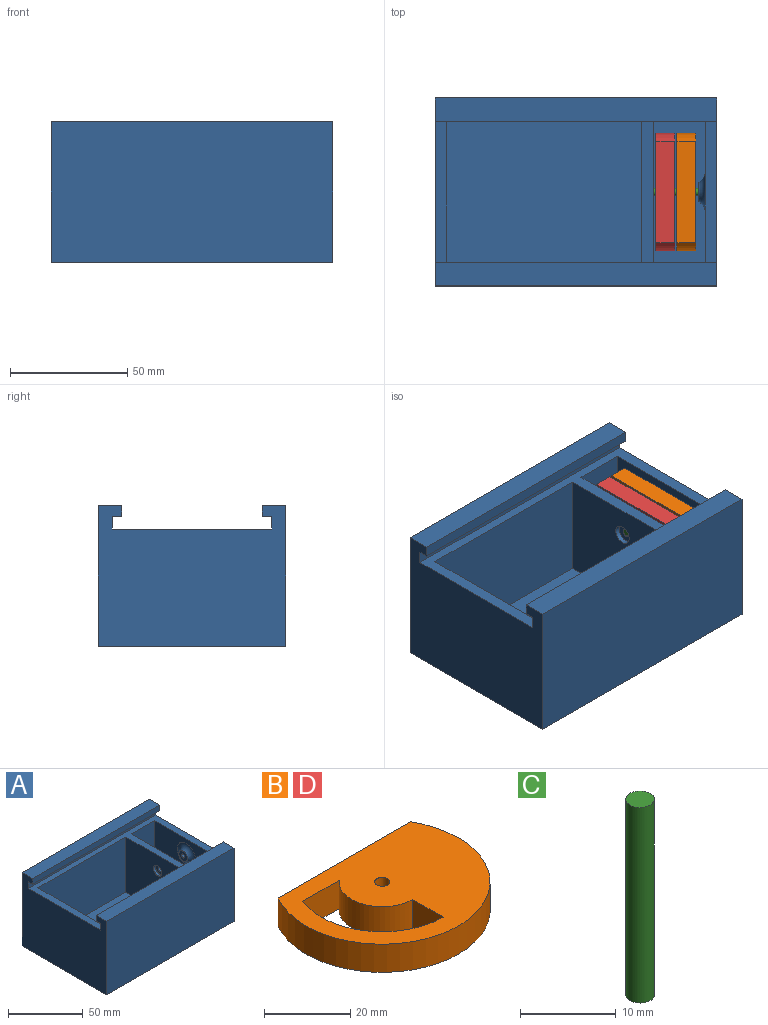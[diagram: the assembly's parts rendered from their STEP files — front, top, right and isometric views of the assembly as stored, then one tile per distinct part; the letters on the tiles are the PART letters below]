
ASSEMBLY  parts=4 mates=3
PART A: 31 faces, bbox 120x80x60 mm
  f0: cylinder r=1.6mm len=3.2mm, axis (-1,0,0), area 30.2mm2, adj f14,f30
  f1: plane 83x45mm, normal (0,1,0), area 3735mm2, adj f7,f9,f13,f15
  f2: plane 45x22mm, normal (0,1,0), area 990mm2, adj f10,f11,f13,f14
  f3: plane 120x4.6mm, normal (0,1,0), area 552mm2, adj f4,f12,f17,f23
  f4: plane 80x60mm, normal (-1,0,0), area 4156.8mm2, adj f3,f8,f13,f16,f17,f18,f19,f20
  f5: plane 83x45mm, normal (0,-1,0), area 3735mm2, adj f7,f9,f13,f15
  f6: plane 45x22mm, normal (0,-1,0), area 990mm2, adj f10,f11,f13,f14
  f7: plane 83x60mm, normal (0,0,1), area 4980mm2, adj f1,f5,f9,f15
  f8: plane 120x80mm, normal (0,0,-1), area 9600mm2, adj f4,f12,f16,f19
  f9: plane 60x45mm, normal (-1,0,0), area 2649.7mm2, adj f1,f5,f7,f13,f29
  f10: plane 60x22mm, normal (0,0,1), area 1320mm2, adj f2,f6,f11,f14
  f11: plane 60x45mm, normal (-1,0,0), area 2468.6mm2, adj f2,f6,f10,f13,f28
  f12: plane 80x60mm, normal (1,0,0), area 4156.8mm2, adj f3,f8,f13,f16,f17,f18,f19,f20
  f13: plane 120x68mm, normal (0,0,1), area 1860mm2, adj f1,f2,f4,f5,f6,f9,f11,f12
  f14: plane 60x45mm, normal (1,0,0), area 2692mm2, adj f0,f2,f6,f10,f13
  f15: plane 60x45mm, normal (1,0,0), area 2700mm2, adj f1,f5,f7,f13
  f16: plane 120x60mm, normal (0,-1,0), area 7200mm2, adj f4,f8,f12,f17
  f17: plane 120x10mm, normal (0,0,1), area 1200mm2, adj f3,f4,f12,f16
  f18: plane 120x4.6mm, normal (0,-1,0), area 552mm2, adj f4,f12,f20,f21
  f19: plane 120x60mm, normal (0,1,0), area 7200mm2, adj f4,f8,f12,f20
  f20: plane 120x10mm, normal (0,0,1), area 1200mm2, adj f4,f12,f18,f19
  f21: plane 120x4mm, normal (0,0,-1), area 480mm2, adj f4,f12,f18,f22
  f22: plane 120x5.4mm, normal (0,-1,0), area 648mm2, adj f4,f12,f13,f21
  f23: plane 120x4mm, normal (0,0,-1), area 480mm2, adj f3,f4,f12,f24
  f24: plane 120x5.4mm, normal (0,1,0), area 648mm2, adj f4,f12,f13,f23
  f25: cylinder r=1.5mm len=3mm, axis (1,0,0), area 28.3mm2, adj f26,f27
  f26: plane 8x8mm, normal (-1,0,0), area 43.2mm2, adj f25,f28
  f27: plane 3x3mm, normal (-1,0,0), area 7.1mm2, adj f25
  f28: torus R=8.58mm, axis (-1,0,0), area 218.3mm2, adj f11,f26
  f29: cylinder r=4mm len=8mm, axis (-1,0,0), area 50.3mm2, adj f9,f30
  f30: plane 8x8mm, normal (-1,0,0), area 42.2mm2, adj f0,f29
PART B: 9 faces, bbox 50x37.5x8 mm
  f0: plane 43.3x8mm, normal (0,1,0), area 346.4mm2, adj f6,f7,f8
  f1: plane 11.93x8mm, normal (0,-1,0), area 95.4mm2, adj f2,f5,f7,f8
  f2: cylinder r=10mm len=17.5mm, axis (0,0,-1), area 193.5mm2, adj f1,f3,f7,f8
  f3: plane 10x8mm, normal (-1,0,0), area 80mm2, adj f2,f5,f7,f8
  f4: cylinder r=1.75mm len=8mm, axis (0,0,-1), area 88mm2, adj f7,f8
  f5: cylinder r=20mm len=27.5mm, axis (0,0,-1), area 312.8mm2, adj f1,f3,f7,f8
  f6: cylinder r=25mm len=50mm, axis (0,0,-1), area 837.8mm2, adj f0,f7,f8
  f7: plane 50x37.5mm, normal (0,0,1), area 1255.2mm2, adj f0,f1,f2,f3,f4,f5,f6
  f8: plane 50x37.5mm, normal (0,0,-1), area 1255.2mm2, adj f0,f1,f2,f3,f4,f5,f6
PART C: 3 faces, bbox 3x3x25 mm
  f0: cylinder r=1.5mm len=25mm, axis (0,0,-1), area 235.6mm2, adj f1,f2
  f1: plane 3x3mm, normal (0,0,1), area 7.1mm2, adj f0
  f2: plane 3x3mm, normal (0,0,-1), area 7.1mm2, adj f0
PART D: same geometry as B
PLACE A t=(-43.9,0,0)mm
PLACE B rot(axis=(0.58,0.58,0.58),120deg) t=(59.1,40,37.5)mm
PLACE C rot(axis=(0,-1,0),90deg) t=(71.1,40,37.5)mm
PLACE D rot(axis=(0.58,-0.58,-0.58),120deg) t=(58.1,40,37.5)mm
MATE revolute B.f4 <-> C.f0  axis (-1,0,0) through (68.1,40,37.5)mm
MATE fastened C.f0 <-> A.f0  axis (-1,0,0) through (46.1,40,37.5)mm
MATE revolute D.f2 <-> C.f0  axis (-1,0,0) through (51.6,40,37.5)mm
